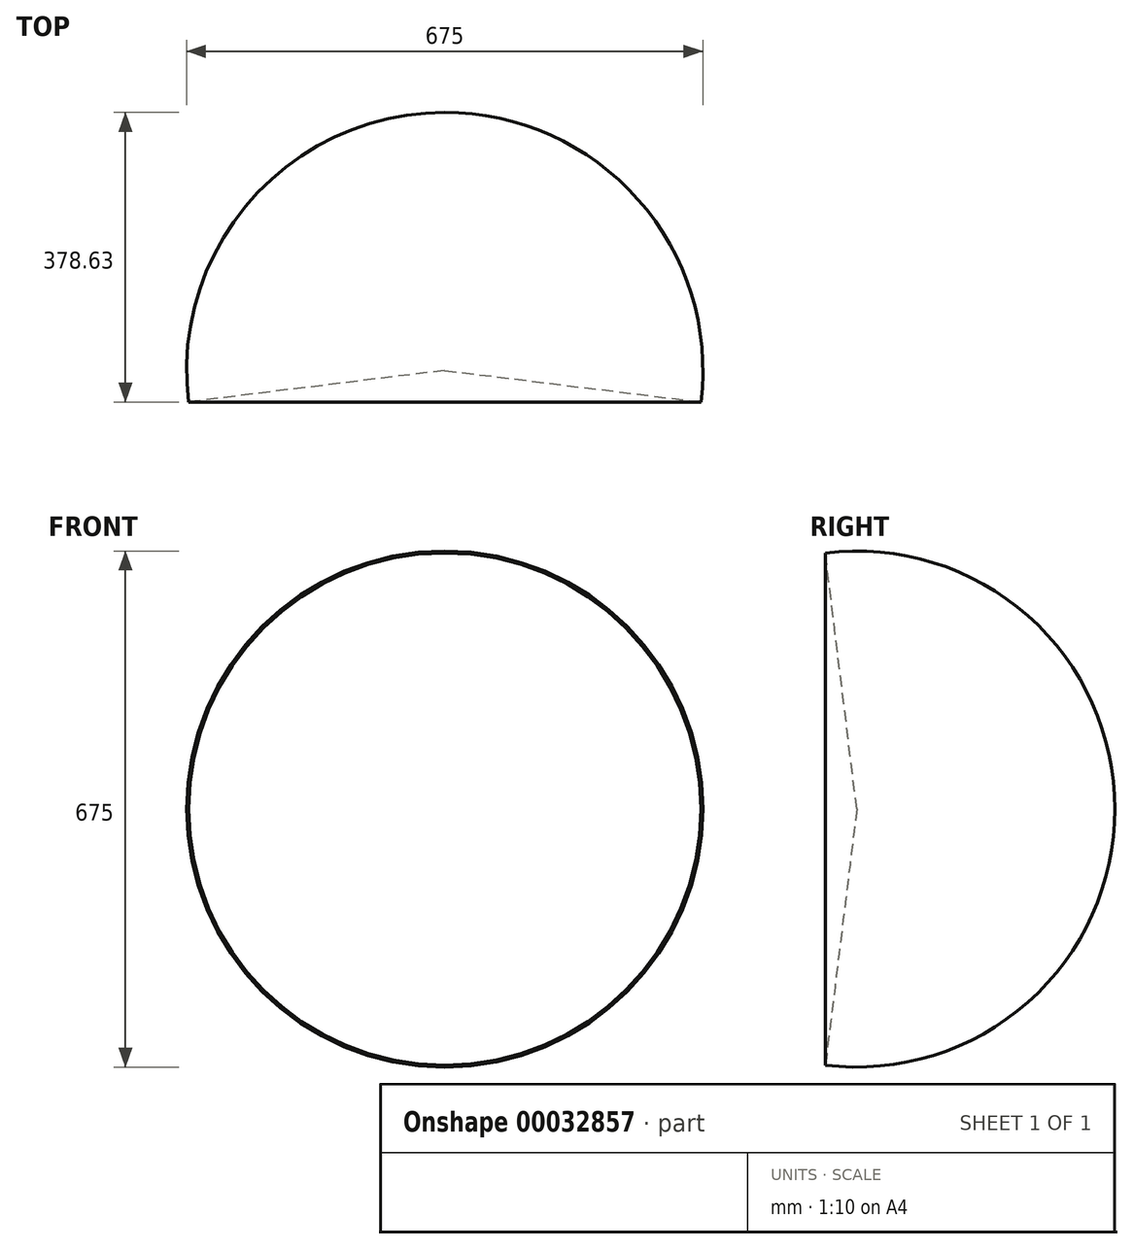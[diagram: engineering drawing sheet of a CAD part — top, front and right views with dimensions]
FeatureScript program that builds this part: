
annotation { "Feature Type Name" : "Feature", "Feature Type Description" : "" }
export const myFeature = defineFeature(function(context is Context, id is Id, definition is map)
    precondition{}
    {
        {
            var Q0;
            Q0=qCreatedBy(makeId("Top.planeOp"),FACE);
            var sketch = newSketch(context, id + "F0", { "sketchPlane" : qUnion([Q0])});
            skArc(sketch, "E0", {"start": v(334.98, -41.13) * mm, "mid": v(0, 337.5) * mm, "end": v(-334.98, -41.13) * mm});
            skLineSegment(sketch, "E1", {"start": v(0, 0) * mm, "end": v(-334.98, -41.13) * mm});
            skLineSegment(sketch, "E2", {"start": v(0, 0) * mm, "end": v(334.98, -41.13) * mm});
            skLineSegment(sketch, "E3", {"start": v(0, 0) * mm, "end": v(0, 337.5) * mm});
            skLineSegment(sketch, "E4", {"start": v(0, 0) * mm, "end": v(356.88, 0) * mm});
            skSolve(sketch);
        }
        {
            var Q0;
            {var subQ1=sQuery(id+"F0.wireOp",EDGE,"E1");Q0=makeQuery(id+"F0.imprint","IMPRINT",FACE,{"disambiguationData":[TD([[makeQuery(id+"F0.imprint","IMPRINT",EDGE,{"derivedFrom":subQ1}),-1.0]])]});}
            var Q1;
            Q1=sQuery(id+"F0.wireOp",EDGE,"E3");
            revolve(context, id + "F1", {"entities" : qUnion([Q0]), "axis" : qUnion([Q1]), "revolveType" : RevolveType.SYMMETRIC, "angle" : 360 * degree});
        }
    });
